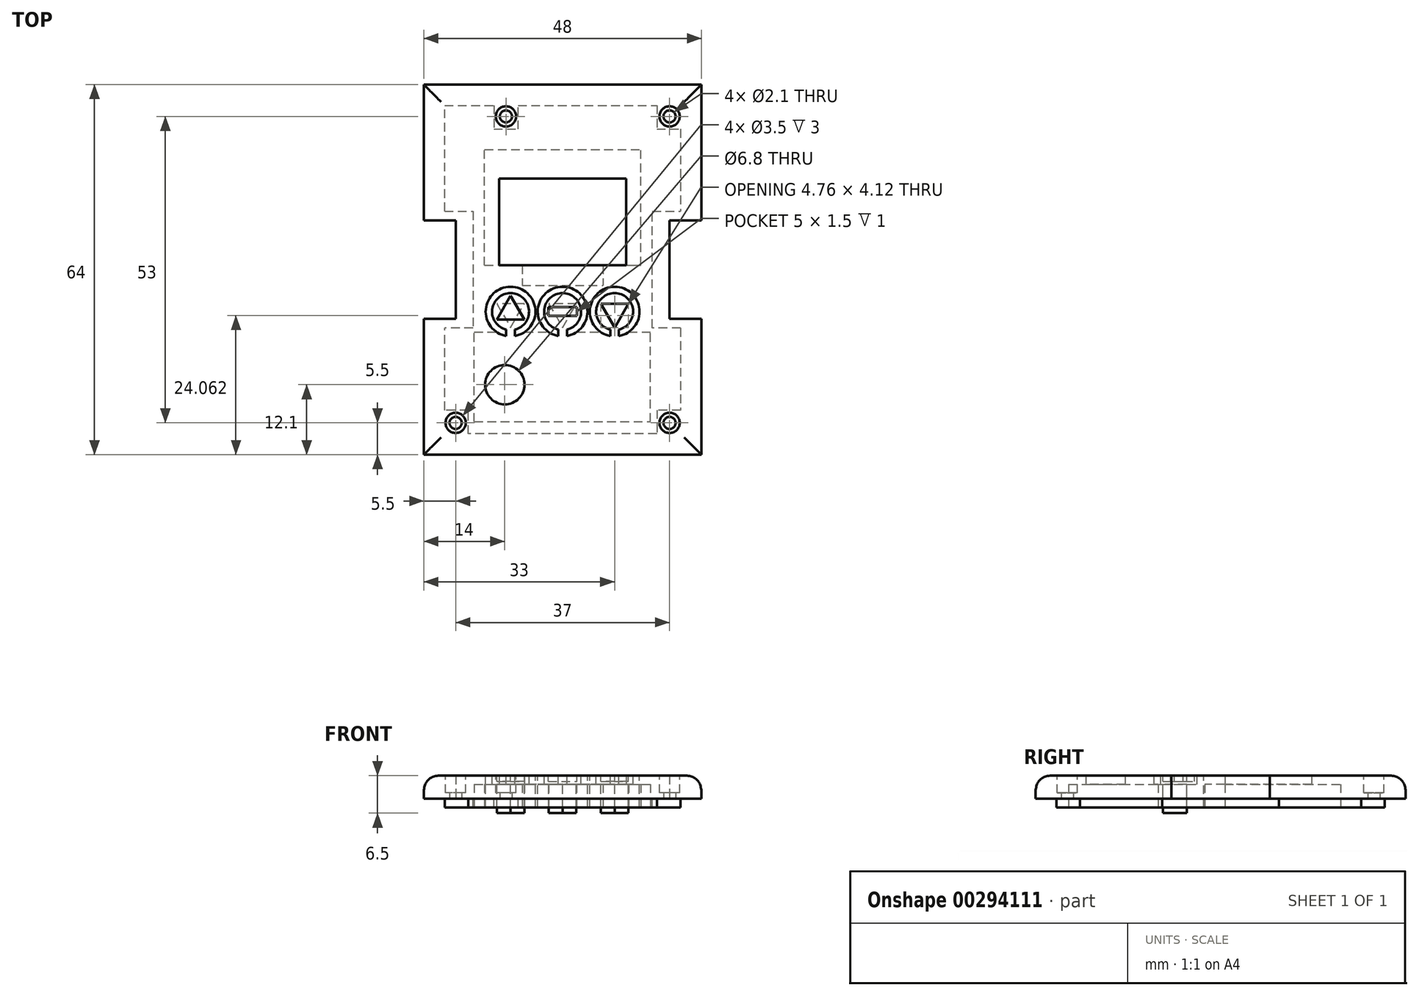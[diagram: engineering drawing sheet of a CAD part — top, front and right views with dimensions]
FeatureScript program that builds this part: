
annotation { "Feature Type Name" : "Feature", "Feature Type Description" : "" }
export const myFeature = defineFeature(function(context is Context, id is Id, definition is map)
    precondition{}
    {
        {
            var Q0;
            Q0=qCreatedBy(makeId("Top.planeOp"),FACE);
            var sketch = newSketch(context, id + "F0", { "sketchPlane" : qUnion([Q0])});
            skLineSegment(sketch, "E0.bottom", {"start": v(-24, 32) * mm, "end": v(24, 32) * mm});
            skLineSegment(sketch, "E0.top", {"start": v(-24, -32) * mm, "end": v(24, -32) * mm});
            skLineSegment(sketch, "E0.left", {"start": v(-24, 32) * mm, "end": v(-24, -32) * mm});
            skLineSegment(sketch, "E0.right", {"start": v(24, 32) * mm, "end": v(24, -32) * mm});
            skSolve(sketch);
        }
        {
            var Q0;
            Q0=makeQuery(id+"F0.imprint","IMPRINT",FACE,{"disambiguationData":[TD([[makeQuery(id+"F0.imprint","IMPRINT",EDGE,{"derivedFrom":sQuery(id+"F0.wireOp",EDGE,"E0.bottom")}),-1.0]])]});
            extrude(context, id + "F1", {"entities" : qUnion([Q0]), "depth" : 4 * mm});
        }
        {
            var Q0;
            Q0=makeQuery(id+"F1.opExtrude","CAP_FACE",FACE,{"disambiguationData":[OSD([sQuery(id+"F0.wireOp",EDGE,"E0.bottom"),sQuery(id+"F0.wireOp",EDGE,"E0.top"),sQuery(id+"F0.wireOp",EDGE,"E0.left"),sQuery(id+"F0.wireOp",EDGE,"E0.right")])],"isStart":true});
            var sketch = newSketch(context, id + "F2", { "sketchPlane" : qUnion([Q0])});
            skLineSegment(sketch, "E1.bottom", {"start": v(-24, 8.5) * mm, "end": v(-18.5, 8.5) * mm});
            skLineSegment(sketch, "E1.top", {"start": v(-24, -8.5) * mm, "end": v(-18.5, -8.5) * mm});
            skLineSegment(sketch, "E1.left", {"start": v(-24, 8.5) * mm, "end": v(-24, -8.5) * mm});
            skLineSegment(sketch, "E1.right", {"start": v(-18.5, 8.5) * mm, "end": v(-18.5, -8.5) * mm});
            skLineSegment(sketch, "E2.bottom", {"start": v(24, 8.5) * mm, "end": v(18.5, 8.5) * mm});
            skLineSegment(sketch, "E2.top", {"start": v(24, -8.5) * mm, "end": v(18.5, -8.5) * mm});
            skLineSegment(sketch, "E2.left", {"start": v(24, 8.5) * mm, "end": v(24, -8.5) * mm});
            skLineSegment(sketch, "E2.right", {"start": v(18.5, 8.5) * mm, "end": v(18.5, -8.5) * mm});
            skSolve(sketch);
        }
        {
            var Q0;
            Q0=qSketchRegion(id+"F2",true);
            extrude(context, id + "F3", {"entities" : qUnion([Q0]), "operationType" : NewBodyOperationType.REMOVE, "endBound" : BoundingType.UP_TO_NEXT, "oppositeDirection" : true, "depth" : 25 * mm});
        }
        {
            var Q0;
            Q0=makeQuery(id+"F1.opExtrude","CAP_FACE",FACE,{"disambiguationData":[OSD([sQuery(id+"F0.wireOp",EDGE,"E0.bottom"),sQuery(id+"F0.wireOp",EDGE,"E0.top"),sQuery(id+"F0.wireOp",EDGE,"E0.left"),sQuery(id+"F0.wireOp",EDGE,"E0.right")])],"isStart":true});
            var sketch = newSketch(context, id + "F4", { "sketchPlane" : qUnion([Q0])});
            skLineSegment(sketch, "E3", {"start": v(-20.4, -28.4) * mm, "end": v(-11.9, -28.4) * mm});
            skLineSegment(sketch, "E4", {"start": v(-11.9, -28.4) * mm, "end": v(-11.9, -24.3) * mm});
            skLineSegment(sketch, "E5", {"start": v(-11.9, -24.3) * mm, "end": v(-7.7, -24.3) * mm});
            skLineSegment(sketch, "E6", {"start": v(-7.7, -24.3) * mm, "end": v(-7.7, -28.4) * mm});
            skLineSegment(sketch, "E7", {"start": v(20.4, 10.1) * mm, "end": v(20.4, 24.3) * mm});
            skLineSegment(sketch, "E8", {"start": v(20.4, 24.3) * mm, "end": v(16.3, 24.3) * mm});
            skLineSegment(sketch, "E9", {"start": v(16.3, 24.3) * mm, "end": v(16.3, 28.4) * mm});
            skLineSegment(sketch, "E10", {"start": v(16.3, 28.4) * mm, "end": v(-16.3, 28.4) * mm});
            skLineSegment(sketch, "E11", {"start": v(-16.3, 28.4) * mm, "end": v(-16.3, 24.3) * mm});
            skLineSegment(sketch, "E12", {"start": v(-16.3, 24.3) * mm, "end": v(-20.4, 24.3) * mm});
            skLineSegment(sketch, "E13", {"start": v(-20.4, 24.3) * mm, "end": v(-20.4, 10.1) * mm});
            skLineSegment(sketch, "E14", {"start": v(-20.4, -10.1) * mm, "end": v(-20.4, -28.4) * mm});
            skLineSegment(sketch, "E15", {"start": v(16.3, -28.4) * mm, "end": v(16.3, -24.3) * mm});
            skLineSegment(sketch, "E16", {"start": v(16.3, -24.3) * mm, "end": v(20.4, -24.3) * mm});
            skLineSegment(sketch, "E17", {"start": v(-7.7, -28.4) * mm, "end": v(16.3, -28.4) * mm});
            skLineSegment(sketch, "E18", {"start": v(20.4, -24.3) * mm, "end": v(20.4, -10.1) * mm});
            skLineSegment(sketch, "E19", {"start": v(20.4, 10.1) * mm, "end": v(15.5, 10.1) * mm});
            skLineSegment(sketch, "E20", {"start": v(15.5, 10.1) * mm, "end": v(15.5, -10.1) * mm});
            skLineSegment(sketch, "E21", {"start": v(15.5, -10.1) * mm, "end": v(20.4, -10.1) * mm});
            skLineSegment(sketch, "E22", {"start": v(-20.4, -10.1) * mm, "end": v(-15.5, -10.1) * mm});
            skLineSegment(sketch, "E23", {"start": v(-15.5, -10.1) * mm, "end": v(-15.5, 10.1) * mm});
            skLineSegment(sketch, "E24", {"start": v(-15.5, 10.1) * mm, "end": v(-20.4, 10.1) * mm});
            skSolve(sketch);
        }
        {
            var Q0;
            Q0=makeQuery(id+"F4.imprint","IMPRINT",FACE,{"disambiguationData":[TD([[makeQuery(id+"F4.imprint","IMPRINT",EDGE,{"derivedFrom":sQuery(id+"F4.wireOp",EDGE,"E3")}),1.0]])]});
            var Q1;
            Q1=makeQuery(id+"F4.imprint","IMPRINT",FACE,{"disambiguationData":[TD([[makeQuery(id+"F4.imprint","IMPRINT",EDGE,{"derivedFrom":sQuery(id+"F4.wireOp",EDGE,"sVbRoeaL-JvD6-wDni-ZTUx-SvIOOkHwP3DD")}),1.0]])]});
            extrude(context, id + "F5", {"entities" : qUnion([Q0, Q1]), "operationType" : NewBodyOperationType.ADD, "depth" : 1.5 * mm});
        }
        {
            var Q0;
            Q0=makeQuery(id+"F1.opExtrude","CAP_FACE",FACE,{"disambiguationData":[OSD([sQuery(id+"F0.wireOp",EDGE,"E0.bottom"),sQuery(id+"F0.wireOp",EDGE,"E0.top"),sQuery(id+"F0.wireOp",EDGE,"E0.left"),sQuery(id+"F0.wireOp",EDGE,"E0.right")])],"isStart":true});
            var sketch = newSketch(context, id + "F6", { "sketchPlane" : qUnion([Q0])});
            skCircle(sketch, "E25", {"center": v(-9.8, -26.5) * mm, "radius": 1.05 * mm});
            skPoint(sketch, "E25.centerSnap0", {"position": v(-9.8, -24.3) * mm});
            skPoint(sketch, "E25.centerSnap1", {"position": v(-7.7, -26.35) * mm});
            skCircle(sketch, "E26", {"center": v(18.5, -26.5) * mm, "radius": 1.05 * mm});
            skPoint(sketch, "E26.centerSnap0", {"position": v(18.35, -24.3) * mm});
            skPoint(sketch, "E26.centerSnap1", {"position": v(16.3, -26.35) * mm});
            skCircle(sketch, "E27", {"center": v(18.5, 26.5) * mm, "radius": 1.05 * mm});
            skPoint(sketch, "E27.centerSnap0", {"position": v(18.35, 24.3) * mm});
            skPoint(sketch, "E27.centerSnap1", {"position": v(16.3, 26.35) * mm});
            skCircle(sketch, "E28", {"center": v(-18.5, 26.5) * mm, "radius": 1.05 * mm});
            skPoint(sketch, "E28.centerSnap0", {"position": v(-16.3, 26.35) * mm});
            skPoint(sketch, "E28.centerSnap1", {"position": v(-18.35, 24.3) * mm});
            skSolve(sketch);
        }
        {
            var Q0;
            Q0=qSketchRegion(id+"F6",true);
            extrude(context, id + "F7", {"entities" : qUnion([Q0]), "operationType" : NewBodyOperationType.REMOVE, "endBound" : BoundingType.UP_TO_NEXT, "oppositeDirection" : true, "depth" : 25 * mm});
        }
        {
            var Q0;
            Q0=makeQuery(id+"F5.opExtrude","CAP_FACE",FACE,{"disambiguationData":[OSD([sQuery(id+"F4.wireOp",EDGE,"E3"),sQuery(id+"F4.wireOp",EDGE,"E4"),sQuery(id+"F4.wireOp",EDGE,"E5"),sQuery(id+"F4.wireOp",EDGE,"E6"),sQuery(id+"F4.wireOp",EDGE,"E7"),sQuery(id+"F4.wireOp",EDGE,"E8"),sQuery(id+"F4.wireOp",EDGE,"E9"),sQuery(id+"F4.wireOp",EDGE,"E10"),sQuery(id+"F4.wireOp",EDGE,"E11"),sQuery(id+"F4.wireOp",EDGE,"E12"),sQuery(id+"F4.wireOp",EDGE,"E13"),sQuery(id+"F4.wireOp",EDGE,"E14"),sQuery(id+"F4.wireOp",EDGE,"E15"),sQuery(id+"F4.wireOp",EDGE,"E16"),sQuery(id+"F4.wireOp",EDGE,"E17"),sQuery(id+"F4.wireOp",EDGE,"E18"),sQuery(id+"F4.wireOp",EDGE,"E19"),sQuery(id+"F4.wireOp",EDGE,"E20"),sQuery(id+"F4.wireOp",EDGE,"E21"),sQuery(id+"F4.wireOp",EDGE,"E22"),sQuery(id+"F4.wireOp",EDGE,"E23"),sQuery(id+"F4.wireOp",EDGE,"E24")])],"isStart":false});
            var sketch = newSketch(context, id + "F8", { "sketchPlane" : qUnion([Q0])});
            skLineSegment(sketch, "E29.bottom", {"start": v(-11, -0.75) * mm, "end": v(11, -0.75) * mm});
            skLineSegment(sketch, "E29.top", {"start": v(-11, -15.75) * mm, "end": v(11, -15.75) * mm});
            skLineSegment(sketch, "E29.left", {"start": v(-11, -0.75) * mm, "end": v(-11, -15.75) * mm});
            skLineSegment(sketch, "E29.right", {"start": v(11, -0.75) * mm, "end": v(11, -15.75) * mm});
            skSolve(sketch);
        }
        {
            var Q0;
            Q0=qSketchRegion(id+"F8",true);
            extrude(context, id + "F9", {"entities" : qUnion([Q0]), "operationType" : NewBodyOperationType.REMOVE, "endBound" : BoundingType.THROUGH_ALL, "oppositeDirection" : true, "depth" : 25 * mm});
        }
        {
            var Q0;
            Q0=makeQuery(id+"F5.opExtrude","CAP_FACE",FACE,{"disambiguationData":[OSD([sQuery(id+"F4.wireOp",EDGE,"E3"),sQuery(id+"F4.wireOp",EDGE,"E4"),sQuery(id+"F4.wireOp",EDGE,"E5"),sQuery(id+"F4.wireOp",EDGE,"E6"),sQuery(id+"F4.wireOp",EDGE,"E7"),sQuery(id+"F4.wireOp",EDGE,"E8"),sQuery(id+"F4.wireOp",EDGE,"E9"),sQuery(id+"F4.wireOp",EDGE,"E10"),sQuery(id+"F4.wireOp",EDGE,"E11"),sQuery(id+"F4.wireOp",EDGE,"E12"),sQuery(id+"F4.wireOp",EDGE,"E13"),sQuery(id+"F4.wireOp",EDGE,"E14"),sQuery(id+"F4.wireOp",EDGE,"E15"),sQuery(id+"F4.wireOp",EDGE,"E16"),sQuery(id+"F4.wireOp",EDGE,"E17"),sQuery(id+"F4.wireOp",EDGE,"E18"),sQuery(id+"F4.wireOp",EDGE,"E19"),sQuery(id+"F4.wireOp",EDGE,"E20"),sQuery(id+"F4.wireOp",EDGE,"E21"),sQuery(id+"F4.wireOp",EDGE,"E22"),sQuery(id+"F4.wireOp",EDGE,"E23"),sQuery(id+"F4.wireOp",EDGE,"E24")])],"isStart":false});
            var sketch = newSketch(context, id + "F10", { "sketchPlane" : qUnion([Q0])});
            skCircle(sketch, "E30", {"center": v(-10, 19.9) * mm, "radius": 3.4 * mm});
            skSolve(sketch);
        }
        {
            var Q0;
            Q0=qSketchRegion(id+"F10",true);
            extrude(context, id + "F11", {"entities" : qUnion([Q0]), "operationType" : NewBodyOperationType.REMOVE, "endBound" : BoundingType.THROUGH_ALL, "oppositeDirection" : true, "depth" : 25 * mm});
        }
        {
            var Q0;
            Q0=makeQuery(id+"F1.opExtrude","CAP_FACE",FACE,{"disambiguationData":[OSD([sQuery(id+"F0.wireOp",EDGE,"E0.bottom"),sQuery(id+"F0.wireOp",EDGE,"E0.top"),sQuery(id+"F0.wireOp",EDGE,"E0.left"),sQuery(id+"F0.wireOp",EDGE,"E0.right")])],"isStart":false});
            var sketch = newSketch(context, id + "F12", { "sketchPlane" : qUnion([Q0])});
            skArc(sketch, "E31", {"start": v(-0.75, -11.48) * mm, "mid": v(0, -2.95) * mm, "end": v(0.75, -11.48) * mm});
            skArc(sketch, "E32", {"start": v(-0.75, -10.36) * mm, "mid": v(0, -4.05) * mm, "end": v(0.75, -10.36) * mm});
            skLineSegment(sketch, "E33", {"start": v(-0.75, -11.48) * mm, "end": v(-0.75, -10.36) * mm});
            skLineSegment(sketch, "E34", {"start": v(0.75, -11.48) * mm, "end": v(0.75, -10.36) * mm});
            skArc(sketch, "E35", {"start": v(8.25, -11.48) * mm, "mid": v(9, -2.95) * mm, "end": v(9.75, -11.48) * mm});
            skArc(sketch, "E36", {"start": v(8.25, -10.36) * mm, "mid": v(9, -4.05) * mm, "end": v(9.75, -10.36) * mm});
            skLineSegment(sketch, "E37", {"start": v(8.25, -11.48) * mm, "end": v(8.25, -10.36) * mm});
            skLineSegment(sketch, "E38", {"start": v(9.75, -11.48) * mm, "end": v(9.75, -10.36) * mm});
            skArc(sketch, "E39", {"start": v(-9.75, -11.48) * mm, "mid": v(-9, -2.95) * mm, "end": v(-8.25, -11.48) * mm});
            skArc(sketch, "E40", {"start": v(-9.75, -10.36) * mm, "mid": v(-9, -4.05) * mm, "end": v(-8.25, -10.36) * mm});
            skLineSegment(sketch, "E41", {"start": v(-9.75, -11.48) * mm, "end": v(-9.75, -10.36) * mm});
            skLineSegment(sketch, "E42", {"start": v(-8.25, -11.48) * mm, "end": v(-8.25, -10.36) * mm});
            skSolve(sketch);
        }
        {
            var Q0;
            Q0=qSketchRegion(id+"F12",true);
            extrude(context, id + "F13", {"entities" : qUnion([Q0]), "operationType" : NewBodyOperationType.REMOVE, "endBound" : BoundingType.THROUGH_ALL, "oppositeDirection" : true, "depth" : 25 * mm});
        }
        {
            var Q0;
            Q0=makeQuery(id+"F5.opExtrude","CAP_FACE",FACE,{"disambiguationData":[OSD([sQuery(id+"F4.wireOp",EDGE,"E3"),sQuery(id+"F4.wireOp",EDGE,"E4"),sQuery(id+"F4.wireOp",EDGE,"E5"),sQuery(id+"F4.wireOp",EDGE,"E6"),sQuery(id+"F4.wireOp",EDGE,"E7"),sQuery(id+"F4.wireOp",EDGE,"E8"),sQuery(id+"F4.wireOp",EDGE,"E9"),sQuery(id+"F4.wireOp",EDGE,"E10"),sQuery(id+"F4.wireOp",EDGE,"E11"),sQuery(id+"F4.wireOp",EDGE,"E12"),sQuery(id+"F4.wireOp",EDGE,"E13"),sQuery(id+"F4.wireOp",EDGE,"E14"),sQuery(id+"F4.wireOp",EDGE,"E15"),sQuery(id+"F4.wireOp",EDGE,"E16"),sQuery(id+"F4.wireOp",EDGE,"E17"),sQuery(id+"F4.wireOp",EDGE,"E18"),sQuery(id+"F4.wireOp",EDGE,"E19"),sQuery(id+"F4.wireOp",EDGE,"E20"),sQuery(id+"F4.wireOp",EDGE,"E21"),sQuery(id+"F4.wireOp",EDGE,"E22"),sQuery(id+"F4.wireOp",EDGE,"E23"),sQuery(id+"F4.wireOp",EDGE,"E24")])],"isStart":false});
            var sketch = newSketch(context, id + "F14", { "sketchPlane" : qUnion([Q0])});
            skLineSegment(sketch, "E43.bottom", {"start": v(-13.5, -0.75) * mm, "end": v(13.5, -0.75) * mm});
            skLineSegment(sketch, "E43.top", {"start": v(-13.5, -20.75) * mm, "end": v(13.5, -20.75) * mm});
            skLineSegment(sketch, "E43.left", {"start": v(-13.5, -0.75) * mm, "end": v(-13.5, -20.75) * mm});
            skLineSegment(sketch, "E43.right", {"start": v(13.5, -0.75) * mm, "end": v(13.5, -20.75) * mm});
            skLineSegment(sketch, "E44.bottom", {"start": v(-7, -0.75) * mm, "end": v(7, -0.75) * mm});
            skLineSegment(sketch, "E44.top", {"start": v(-7, 2.75) * mm, "end": v(7, 2.75) * mm});
            skLineSegment(sketch, "E44.left", {"start": v(-7, -0.75) * mm, "end": v(-7, 2.75) * mm});
            skLineSegment(sketch, "E44.right", {"start": v(7, -0.75) * mm, "end": v(7, 2.75) * mm});
            skSolve(sketch);
        }
        {
            var Q0;
            Q0=qSketchRegion(id+"F14",true);
            extrude(context, id + "F15", {"entities" : qUnion([Q0]), "operationType" : NewBodyOperationType.REMOVE, "oppositeDirection" : true, "depth" : 4 * mm});
        }
        {
            var Q0;
            Q0=makeQuery(id+"F1.opExtrude","CAP_FACE",FACE,{"disambiguationData":[OSD([sQuery(id+"F0.wireOp",EDGE,"E0.bottom"),sQuery(id+"F0.wireOp",EDGE,"E0.top"),sQuery(id+"F0.wireOp",EDGE,"E0.left"),sQuery(id+"F0.wireOp",EDGE,"E0.right")])],"isStart":false});
            var sketch = newSketch(context, id + "F16", { "sketchPlane" : qUnion([Q0])});
            skCircle(sketch, "E45.cCircle", {"center": v(9, -7.25) * mm, "radius": 2.75 * mm, "construction": true});
            skLineSegment(sketch, "E45.0", {"start": v(6.62, -5.87) * mm, "end": v(11.38, -5.87) * mm});
            skLineSegment(sketch, "E45.1", {"start": v(11.38, -5.87) * mm, "end": v(9, -10) * mm});
            skLineSegment(sketch, "E45.2", {"start": v(9, -10) * mm, "end": v(6.62, -5.87) * mm});
            skCircle(sketch, "E46.cCircle", {"center": v(-9, -7.25) * mm, "radius": 2.75 * mm, "construction": true});
            skLineSegment(sketch, "E46.0", {"start": v(-11.38, -8.62) * mm, "end": v(-9, -4.5) * mm});
            skLineSegment(sketch, "E46.1", {"start": v(-9, -4.5) * mm, "end": v(-6.62, -8.62) * mm});
            skLineSegment(sketch, "E46.2", {"start": v(-6.62, -8.62) * mm, "end": v(-11.38, -8.62) * mm});
            skLineSegment(sketch, "E47.bottom", {"start": v(-2.5, -8) * mm, "end": v(2.5, -8) * mm});
            skLineSegment(sketch, "E47.top", {"start": v(-2.5, -6.5) * mm, "end": v(2.5, -6.5) * mm});
            skLineSegment(sketch, "E47.left", {"start": v(-2.5, -8) * mm, "end": v(-2.5, -6.5) * mm});
            skLineSegment(sketch, "E47.right", {"start": v(2.5, -8) * mm, "end": v(2.5, -6.5) * mm});
            skPoint(sketch, "E47.middle", {"position": v(0, -7.25) * mm});
            skSolve(sketch);
        }
        {
            var Q0;
            Q0=qSketchRegion(id+"F16",true);
            extrude(context, id + "F17", {"entities" : qUnion([Q0]), "operationType" : NewBodyOperationType.REMOVE, "oppositeDirection" : true, "depth" : 1 * mm});
        }
        {
            var Q0;
            Q0=makeQuery(id+"F5.opExtrude","CAP_FACE",FACE,{"disambiguationData":[OSD([sQuery(id+"F4.wireOp",EDGE,"E3"),sQuery(id+"F4.wireOp",EDGE,"E4"),sQuery(id+"F4.wireOp",EDGE,"E5"),sQuery(id+"F4.wireOp",EDGE,"E6"),sQuery(id+"F4.wireOp",EDGE,"E7"),sQuery(id+"F4.wireOp",EDGE,"E8"),sQuery(id+"F4.wireOp",EDGE,"E9"),sQuery(id+"F4.wireOp",EDGE,"E10"),sQuery(id+"F4.wireOp",EDGE,"E11"),sQuery(id+"F4.wireOp",EDGE,"E12"),sQuery(id+"F4.wireOp",EDGE,"E13"),sQuery(id+"F4.wireOp",EDGE,"E14"),sQuery(id+"F4.wireOp",EDGE,"E15"),sQuery(id+"F4.wireOp",EDGE,"E16"),sQuery(id+"F4.wireOp",EDGE,"E17"),sQuery(id+"F4.wireOp",EDGE,"E18"),sQuery(id+"F4.wireOp",EDGE,"E19"),sQuery(id+"F4.wireOp",EDGE,"E20"),sQuery(id+"F4.wireOp",EDGE,"E21"),sQuery(id+"F4.wireOp",EDGE,"E22"),sQuery(id+"F4.wireOp",EDGE,"E23"),sQuery(id+"F4.wireOp",EDGE,"E24")])],"isStart":false});
            var sketch = newSketch(context, id + "F18", { "sketchPlane" : qUnion([Q0])});
            skCircle(sketch, "E48", {"center": v(-9, 7.25) * mm, "radius": 4.3 * mm});
            skCircle(sketch, "E49", {"center": v(0, 7.25) * mm, "radius": 4.3 * mm});
            skCircle(sketch, "E50", {"center": v(9, 7.25) * mm, "radius": 4.3 * mm});
            skLineSegment(sketch, "E51.bottom", {"start": v(-15.3, 26.3) * mm, "end": v(15.2, 26.3) * mm});
            skLineSegment(sketch, "E51.top", {"start": v(-15.3, 10.8) * mm, "end": v(15.2, 10.8) * mm});
            skLineSegment(sketch, "E51.left", {"start": v(-15.3, 26.3) * mm, "end": v(-15.3, 10.8) * mm});
            skLineSegment(sketch, "E51.right", {"start": v(15.2, 26.3) * mm, "end": v(15.2, 10.8) * mm});
            skSolve(sketch);
        }
        {
            var Q0;
            Q0=qSketchRegion(id+"F18",true);
            extrude(context, id + "F19", {"entities" : qUnion([Q0]), "operationType" : NewBodyOperationType.REMOVE, "oppositeDirection" : true, "depth" : 4 * mm});
        }
        {
            var Q0;
            Q0=makeQuery(id+"F19.boolean.opBoolean","COPY",FACE,{"derivedFrom":makeQuery(id+"F19.opExtrude","CAP_FACE",FACE,{"disambiguationData":[OSD([sQuery(id+"F18.wireOp",EDGE,"E50")])],"isStart":false})});
            var sketch = newSketch(context, id + "F20", { "sketchPlane" : qUnion([Q0])});
            skCircle(sketch, "E52.cCircle", {"center": v(9, 7.25) * mm, "radius": 2.75 * mm, "construction": true});
            skLineSegment(sketch, "E52.0", {"start": v(11.38, 5.87) * mm, "end": v(6.62, 5.87) * mm});
            skLineSegment(sketch, "E52.1", {"start": v(6.62, 5.87) * mm, "end": v(9, 10) * mm});
            skLineSegment(sketch, "E52.2", {"start": v(9, 10) * mm, "end": v(11.38, 5.87) * mm});
            skCircle(sketch, "E53.cCircle", {"center": v(0, 7.25) * mm, "radius": 2.75 * mm, "construction": true});
            skLineSegment(sketch, "E53.0", {"start": v(2.38, 5.87) * mm, "end": v(-2.38, 5.87) * mm});
            skLineSegment(sketch, "E53.1", {"start": v(-2.38, 5.87) * mm, "end": v(0, 10) * mm});
            skLineSegment(sketch, "E53.2", {"start": v(0, 10) * mm, "end": v(2.38, 5.87) * mm});
            skCircle(sketch, "E54.cCircle", {"center": v(-9, 7.25) * mm, "radius": 2.75 * mm, "construction": true});
            skLineSegment(sketch, "E54.0", {"start": v(-6.62, 5.87) * mm, "end": v(-11.38, 5.87) * mm});
            skLineSegment(sketch, "E54.1", {"start": v(-11.38, 5.87) * mm, "end": v(-9, 10) * mm});
            skLineSegment(sketch, "E54.2", {"start": v(-9, 10) * mm, "end": v(-6.62, 5.87) * mm});
            skSolve(sketch);
        }
        {
            var Q0;
            Q0=qSketchRegion(id+"F20",true);
            extrude(context, id + "F21", {"entities" : qUnion([Q0]), "operationType" : NewBodyOperationType.ADD, "depth" : 5 * mm});
        }
        {
            var Q0;
            Q0=makeQuery(id+"F1.opExtrude","CAP_EDGE",EDGE,{"disambiguationData":[OSD([sQuery(id+"F0.wireOp",EDGE,"E0.top")])],"isStart":false});
            var Q1;
            {var subQ0=sQuery(id+"F0.wireOp",EDGE,"E0.right");var subQ1=sQuery(id+"F0.wireOp",EDGE,"E0.top");Q1=makeQuery(id+"F3.boolean.opBoolean","SPLIT",EDGE,{"disambiguationData":[TD([makeQuery(id+"F1.opExtrude","SWEPT_FACE",FACE,{"disambiguationData":[OSD([subQ1])]})])],"derivedFrom":makeQuery(id+"F1.opExtrude","CAP_EDGE",EDGE,{"disambiguationData":[OSD([subQ0])],"isStart":false})});}
            var Q2;
            Q2=makeQuery(id+"F3.boolean.opBoolean","COPY",EDGE,{"derivedFrom":makeQuery(id+"F3.opExtrude","CAP_EDGE",EDGE,{"disambiguationData":[OSD([sQuery(id+"F2.wireOp",EDGE,"E2.bottom")])],"isStart":false})});
            var Q3;
            Q3=makeQuery(id+"F3.boolean.opBoolean","COPY",EDGE,{"derivedFrom":makeQuery(id+"F3.opExtrude","CAP_EDGE",EDGE,{"disambiguationData":[OSD([sQuery(id+"F2.wireOp",EDGE,"E2.right")])],"isStart":false})});
            var Q4;
            Q4=makeQuery(id+"F3.boolean.opBoolean","COPY",EDGE,{"derivedFrom":makeQuery(id+"F3.opExtrude","CAP_EDGE",EDGE,{"disambiguationData":[OSD([sQuery(id+"F2.wireOp",EDGE,"E2.top")])],"isStart":false})});
            var Q5;
            {var subQ0=sQuery(id+"F0.wireOp",EDGE,"E0.bottom");var subQ1=sQuery(id+"F0.wireOp",EDGE,"E0.right");Q5=makeQuery(id+"F3.boolean.opBoolean","SPLIT",EDGE,{"disambiguationData":[TD([makeQuery(id+"F1.opExtrude","SWEPT_FACE",FACE,{"disambiguationData":[OSD([subQ0])]})])],"derivedFrom":makeQuery(id+"F1.opExtrude","CAP_EDGE",EDGE,{"disambiguationData":[OSD([subQ1])],"isStart":false})});}
            var Q6;
            Q6=makeQuery(id+"F1.opExtrude","CAP_EDGE",EDGE,{"disambiguationData":[OSD([sQuery(id+"F0.wireOp",EDGE,"E0.bottom")])],"isStart":false});
            var Q7;
            {var subQ0=sQuery(id+"F0.wireOp",EDGE,"E0.bottom");var subQ1=sQuery(id+"F0.wireOp",EDGE,"E0.left");Q7=makeQuery(id+"F3.boolean.opBoolean","SPLIT",EDGE,{"disambiguationData":[TD([makeQuery(id+"F1.opExtrude","SWEPT_FACE",FACE,{"disambiguationData":[OSD([subQ0])]})])],"derivedFrom":makeQuery(id+"F1.opExtrude","CAP_EDGE",EDGE,{"disambiguationData":[OSD([subQ1])],"isStart":false})});}
            var Q8;
            Q8=makeQuery(id+"F3.boolean.opBoolean","COPY",EDGE,{"derivedFrom":makeQuery(id+"F3.opExtrude","CAP_EDGE",EDGE,{"disambiguationData":[OSD([sQuery(id+"F2.wireOp",EDGE,"E1.top")])],"isStart":false})});
            var Q9;
            Q9=makeQuery(id+"F3.boolean.opBoolean","COPY",EDGE,{"derivedFrom":makeQuery(id+"F3.opExtrude","CAP_EDGE",EDGE,{"disambiguationData":[OSD([sQuery(id+"F2.wireOp",EDGE,"E1.right")])],"isStart":false})});
            var Q10;
            Q10=makeQuery(id+"F3.boolean.opBoolean","COPY",EDGE,{"derivedFrom":makeQuery(id+"F3.opExtrude","CAP_EDGE",EDGE,{"disambiguationData":[OSD([sQuery(id+"F2.wireOp",EDGE,"E1.bottom")])],"isStart":false})});
            var Q11;
            {var subQ0=sQuery(id+"F0.wireOp",EDGE,"E0.left");var subQ1=sQuery(id+"F0.wireOp",EDGE,"E0.top");Q11=makeQuery(id+"F3.boolean.opBoolean","SPLIT",EDGE,{"disambiguationData":[TD([makeQuery(id+"F1.opExtrude","SWEPT_FACE",FACE,{"disambiguationData":[OSD([subQ1])]})])],"derivedFrom":makeQuery(id+"F1.opExtrude","CAP_EDGE",EDGE,{"disambiguationData":[OSD([subQ0])],"isStart":false})});}
            fillet(context, id + "F22", {"entities" : qUnion([Q0, Q1, Q2, Q3, Q4, Q5, Q6, Q7, Q8, Q9, Q10, Q11]), "radius" : 3 * mm, "tangentPropagation" : true, "rho" : 0.5, "crossSection" : FilletCrossSection.CONIC, "allowEdgeOverflow" : false});
        }
        {
            var Q0;
            Q0=makeQuery(id+"F1.opExtrude","CAP_FACE",FACE,{"disambiguationData":[OSD([sQuery(id+"F0.wireOp",EDGE,"E0.bottom"),sQuery(id+"F0.wireOp",EDGE,"E0.top"),sQuery(id+"F0.wireOp",EDGE,"E0.left"),sQuery(id+"F0.wireOp",EDGE,"E0.right")])],"isStart":false});
            var sketch = newSketch(context, id + "F23", { "sketchPlane" : qUnion([Q0])});
            skCircle(sketch, "E55", {"center": v(-9.8, 26.5) * mm, "radius": 1.75 * mm});
            skCircle(sketch, "E56", {"center": v(18.5, 26.5) * mm, "radius": 1.75 * mm});
            skCircle(sketch, "E57", {"center": v(-18.5, -26.5) * mm, "radius": 1.75 * mm});
            skCircle(sketch, "E58", {"center": v(18.5, -26.5) * mm, "radius": 1.75 * mm});
            skSolve(sketch);
        }
        {
            var Q0;
            Q0=qSketchRegion(id+"F23",true);
            extrude(context, id + "F24", {"entities" : qUnion([Q0]), "operationType" : NewBodyOperationType.REMOVE, "oppositeDirection" : true, "depth" : 3 * mm});
        }
    });
